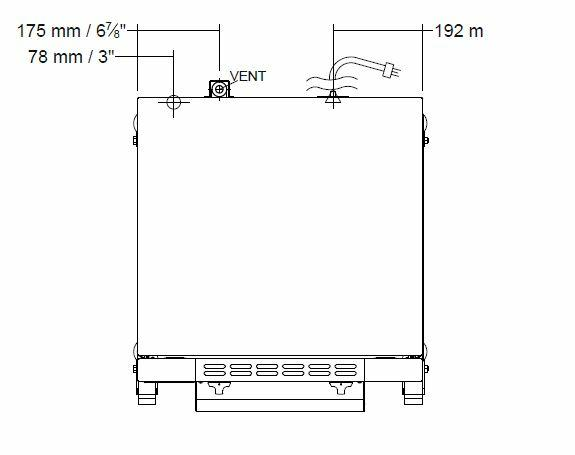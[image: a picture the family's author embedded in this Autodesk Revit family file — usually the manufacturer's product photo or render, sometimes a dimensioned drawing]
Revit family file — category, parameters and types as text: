
# Revit family: QF_MOFFAT_E30M3-SK2731N_NZ
name_source: partatom
category: Specialty Equipment
revit_build: Autodesk Revit 2014 (Build: 20130308_1515(x64)
units: mm (PartAtom-declared; Revit-internal decimal feet)

## types (1)
- QF_MOFFAT_E30M3-SK2731N_NZ
    Apparent Power = 2280 VA
    Conn Conduit = Yes
    Depth = 665 mm  [stored 2.18176 ft]
    Description = GN 1/1 MANUAL / ELECTRIC CONVECTION OVEN ON A STAINLESS STEEL STAND
    Elec Conn Connection Height = 0 mm  [stored 0 ft]
    Elec Conn RI Height = 0 mm  [stored 0 ft]
    Electrical Remarks = 230-240V, 50Hz, 1P+N+E, 2.3kW, 9.5A
    Exhaust RI Height = 0 mm  [stored 0 ft]
    Exhaust Static Press = 0.00 in-wg
    Exhaust Vent Depth = 0 mm  [stored 0 ft]
    Exhaust Vent Diameter = 0 mm  [stored 0 ft]
    Exhaust Vent Width = 0 mm  [stored 0 ft]
    Exhaust Volume = 0 CFM
    FL Amps = 10 A
    Foodservice Equipment Identifier = Yes
    Height = 1508 mm  [stored 4.94751 ft]
    Height of Stand = 880 mm  [stored 2.88714 ft]
    Identify Quantity as Lot = Yes
    Length = 810 mm
    Manufacturer = MOFFAT
    Max Overcurrent Protection = 0 A
    Min Ckt Ampacity = 0 A
    Model = E30M3-SK2731N
    Number of Poles = 1
    Phase = 1
    Volts = 240 V
    Watts = 2300 W
    Weight in Pounds = 0

note: [stored X ft] marks values corroborated as IEEE doubles in the binary element streams (Revit-internal decimal feet)

## geometry (parser evidence)
native form markers: Blend x12, Sweep x13
no freeform markers — native parametric forms only
